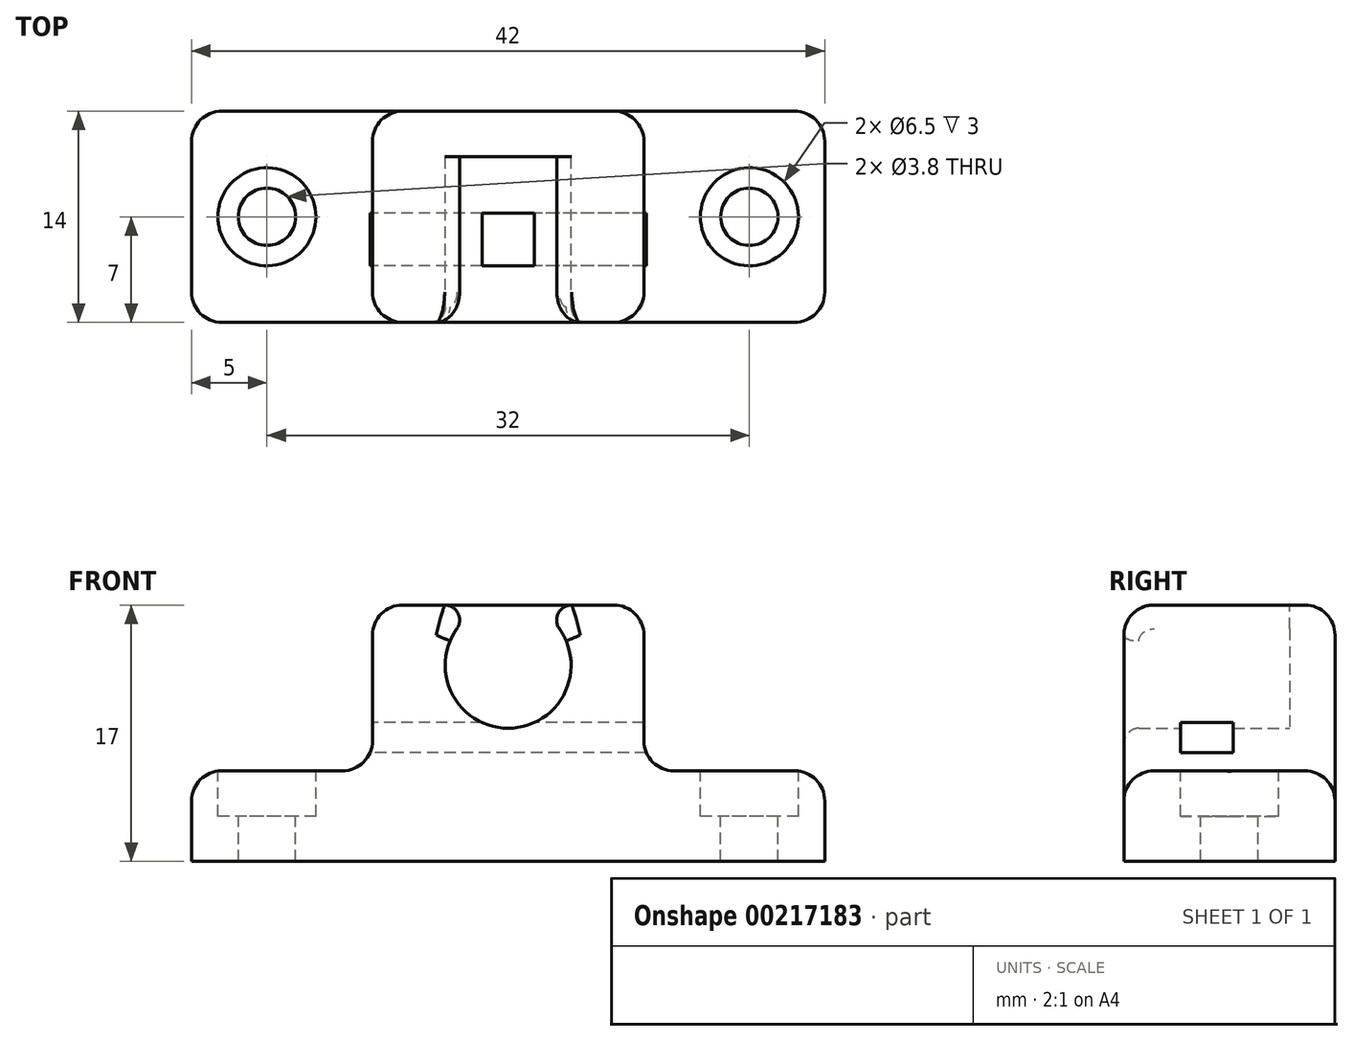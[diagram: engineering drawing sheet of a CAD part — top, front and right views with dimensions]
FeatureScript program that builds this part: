
annotation { "Feature Type Name" : "Feature", "Feature Type Description" : "" }
export const myFeature = defineFeature(function(context is Context, id is Id, definition is map)
    precondition{}
    {
        {
            var Q0;
            Q0=qCreatedBy(makeId("Front.planeOp"),FACE);
            var sketch = newSketch(context, id + "F0", { "sketchPlane" : qUnion([Q0])});
            skLineSegment(sketch, "E0", {"start": v(0, 0) * mm, "end": v(-21, 0) * mm});
            skLineSegment(sketch, "E1", {"start": v(-21, 0) * mm, "end": v(-21, 6) * mm});
            skLineSegment(sketch, "E2", {"start": v(-21, 6) * mm, "end": v(-9, 6) * mm});
            skLineSegment(sketch, "E3", {"start": v(-9, 6) * mm, "end": v(-9, 17) * mm});
            skLineSegment(sketch, "E4", {"start": v(-9, 17) * mm, "end": v(0, 17) * mm});
            skLineSegment(sketch, "E5.MirrorCS", {"start": v(0, 0) * mm, "end": v(21, 0) * mm});
            skLineSegment(sketch, "E6.MirrorCS", {"start": v(21, 6) * mm, "end": v(9, 6) * mm});
            skLineSegment(sketch, "E7.MirrorCS", {"start": v(9, 17) * mm, "end": v(0, 17) * mm});
            skLineSegment(sketch, "E8.MirrorCS", {"start": v(9, 6) * mm, "end": v(9, 17) * mm});
            skLineSegment(sketch, "E9.MirrorCS", {"start": v(21, 0) * mm, "end": v(21, 6) * mm});
            skCircle(sketch, "E10", {"center": v(0, 13) * mm, "radius": 4.17 * mm});
            skSolve(sketch);
        }
        {
            var Q0;
            Q0=makeQuery(id+"F0.imprint","IMPRINT",FACE,{"disambiguationData":[TD([[makeQuery(id+"F0.imprint","IMPRINT",EDGE,{"derivedFrom":sQuery(id+"F0.wireOp",EDGE,"E0")}),-1.0]])]});
            var Q1;
            {var subQ0=sQuery(id+"F0.wireOp",EDGE,"E7.MirrorCS");var subQ1=sQuery(id+"F0.wireOp",EDGE,"E4");var subQ2=makeQuery(id+"F0.imprint","INTERSECT",VERTEX,{"derivedFrom":[subQ1,subQ0]});Q1=makeQuery(id+"F0.imprint","IMPRINT",FACE,{"disambiguationData":[TD([[makeQuery(id+"F0.imprint","IMPRINT",EDGE,{"disambiguationData":[TD([[subQ2,1.0]])],"derivedFrom":subQ1}),-1.0]])]});}
            extrude(context, id + "F1", {"entities" : qUnion([Q0, Q1]), "oppositeDirection" : true, "depth" : 3 * mm});
        }
        {
            var Q0;
            Q0=makeQuery(id+"F0.imprint","IMPRINT",FACE,{"disambiguationData":[TD([[makeQuery(id+"F0.imprint","IMPRINT",EDGE,{"derivedFrom":sQuery(id+"F0.wireOp",EDGE,"E0")}),-1.0]])]});
            extrude(context, id + "F2", {"entities" : qUnion([Q0]), "operationType" : NewBodyOperationType.ADD, "depth" : 11 * mm});
        }
        {
            var Q0;
            {var subQ0=sQuery(id+"F0.wireOp",EDGE,"E3");Q0=makeQuery(id+"F2.boolean.opBoolean","MERGE",FACE,{"derivedFrom":[makeQuery(id+"F1.opExtrude","SWEPT_FACE",FACE,{"disambiguationData":[OSD([subQ0])]}),makeQuery(id+"F2.opExtrude","SWEPT_FACE",FACE,{"disambiguationData":[OSD([subQ0])]})]});}
            var sketch = newSketch(context, id + "F3", { "sketchPlane" : qUnion([Q0])});
            skLineSegment(sketch, "E11.bottom", {"start": v(3.75, 9.2) * mm, "end": v(7.25, 9.2) * mm});
            skLineSegment(sketch, "E11.top", {"start": v(3.75, 7.2) * mm, "end": v(7.25, 7.2) * mm});
            skLineSegment(sketch, "E11.left", {"start": v(3.75, 9.2) * mm, "end": v(3.75, 7.2) * mm});
            skLineSegment(sketch, "E11.right", {"start": v(7.25, 9.2) * mm, "end": v(7.25, 7.2) * mm});
            skSolve(sketch);
        }
        {
            var Q0;
            Q0=makeQuery(id+"F3.imprint","IMPRINT",FACE,{"disambiguationData":[TD([[makeQuery(id+"F3.imprint","IMPRINT",EDGE,{"derivedFrom":sQuery(id+"F3.wireOp",EDGE,"E11.bottom")}),-1.0]])]});
            extrude(context, id + "F4", {"entities" : qUnion([Q0]), "operationType" : NewBodyOperationType.REMOVE, "endBound" : BoundingType.THROUGH_ALL, "oppositeDirection" : true, "depth" : 25 * mm});
        }
        {
            var Q0;
            {var subQ0=sQuery(id+"F0.wireOp",EDGE,"E2");Q0=makeQuery(id+"F2.boolean.opBoolean","MERGE",FACE,{"derivedFrom":[makeQuery(id+"F1.opExtrude","SWEPT_FACE",FACE,{"disambiguationData":[OSD([subQ0])]}),makeQuery(id+"F2.opExtrude","SWEPT_FACE",FACE,{"disambiguationData":[OSD([subQ0])]})]});}
            var sketch = newSketch(context, id + "F5", { "sketchPlane" : qUnion([Q0])});
            skCircle(sketch, "E12", {"center": v(-16, -4) * mm, "radius": 3.25 * mm});
            skPoint(sketch, "E12.centerSnap0", {"position": v(-21, -4) * mm});
            skCircle(sketch, "E13", {"center": v(-16, -4) * mm, "radius": 1.9 * mm});
            skSolve(sketch);
        }
        {
            var Q0;
            {var subQ0=sQuery(id+"F0.wireOp",EDGE,"E6.MirrorCS");Q0=makeQuery(id+"F2.boolean.opBoolean","MERGE",FACE,{"derivedFrom":[makeQuery(id+"F1.opExtrude","SWEPT_FACE",FACE,{"disambiguationData":[OSD([subQ0])]}),makeQuery(id+"F2.opExtrude","SWEPT_FACE",FACE,{"disambiguationData":[OSD([subQ0])]})]});}
            var sketch = newSketch(context, id + "F6", { "sketchPlane" : qUnion([Q0])});
            skCircle(sketch, "E14", {"center": v(16, -4) * mm, "radius": 3.25 * mm});
            skPoint(sketch, "E14.centerSnap0", {"position": v(21, -4) * mm});
            skCircle(sketch, "E15", {"center": v(16, -4) * mm, "radius": 1.9 * mm});
            skSolve(sketch);
        }
        {
            var Q0;
            Q0=makeQuery(id+"F5.imprint","IMPRINT",FACE,{"disambiguationData":[TD([[makeQuery(id+"F5.imprint","IMPRINT",EDGE,{"derivedFrom":sQuery(id+"F5.wireOp",EDGE,"E12")}),1.0]])]});
            var Q1;
            Q1=makeQuery(id+"F6.imprint","IMPRINT",FACE,{"disambiguationData":[TD([[makeQuery(id+"F6.imprint","IMPRINT",EDGE,{"derivedFrom":sQuery(id+"F6.wireOp",EDGE,"E14")}),1.0]])]});
            extrude(context, id + "F7", {"entities" : qUnion([Q0, Q1]), "operationType" : NewBodyOperationType.REMOVE, "oppositeDirection" : true, "depth" : 3 * mm});
        }
        {
            var Q0;
            {var subQ0=sQuery(id+"F0.wireOp",EDGE,"E2");Q0=makeQuery(id+"F7.boolean.opBoolean","SPLIT",FACE,{"disambiguationData":[TD([makeQuery(id+"F7.opExtrude","SWEPT_FACE",FACE,{"disambiguationData":[OSD([sQuery(id+"F5.wireOp",EDGE,"E13")])]})])],"derivedFrom":makeQuery(id+"F2.boolean.opBoolean","MERGE",FACE,{"derivedFrom":[makeQuery(id+"F1.opExtrude","SWEPT_FACE",FACE,{"disambiguationData":[OSD([subQ0])]}),makeQuery(id+"F2.opExtrude","SWEPT_FACE",FACE,{"disambiguationData":[OSD([subQ0])]})]})});}
            var Q1;
            {var subQ0=sQuery(id+"F0.wireOp",EDGE,"E6.MirrorCS");Q1=makeQuery(id+"F7.boolean.opBoolean","SPLIT",FACE,{"disambiguationData":[TD([makeQuery(id+"F7.opExtrude","SWEPT_FACE",FACE,{"disambiguationData":[OSD([sQuery(id+"F6.wireOp",EDGE,"E15")])]})])],"derivedFrom":makeQuery(id+"F2.boolean.opBoolean","MERGE",FACE,{"derivedFrom":[makeQuery(id+"F1.opExtrude","SWEPT_FACE",FACE,{"disambiguationData":[OSD([subQ0])]}),makeQuery(id+"F2.opExtrude","SWEPT_FACE",FACE,{"disambiguationData":[OSD([subQ0])]})]})});}
            extrude(context, id + "F8", {"entities" : qUnion([Q0, Q1]), "operationType" : NewBodyOperationType.REMOVE, "oppositeDirection" : true, "depth" : 25 * mm});
        }
        {
            var Q0;
            Q0=makeQuery(id+"F2.opExtrude","CAP_EDGE",EDGE,{"disambiguationData":[OSD([sQuery(id+"F0.wireOp",EDGE,"E1")])],"isStart":false});
            var Q1;
            Q1=makeQuery(id+"F2.opExtrude","CAP_EDGE",EDGE,{"disambiguationData":[OSD([sQuery(id+"F0.wireOp",EDGE,"E2")])],"isStart":false});
            var Q2;
            Q2=makeQuery(id+"F2.opExtrude","CAP_EDGE",EDGE,{"disambiguationData":[OSD([sQuery(id+"F0.wireOp",EDGE,"E3")])],"isStart":false});
            var Q3;
            Q3=makeQuery(id+"F2.opExtrude","CAP_EDGE",EDGE,{"disambiguationData":[OSD([sQuery(id+"F0.wireOp",EDGE,"E4")])],"isStart":false});
            var Q4;
            {var subQ0=sQuery(id+"F0.wireOp",EDGE,"E4");var subQ1=sQuery(id+"F0.wireOp",EDGE,"E3");Q4=makeQuery(id+"F2.boolean.opBoolean","MERGE",EDGE,{"derivedFrom":[makeQuery(id+"F1.opExtrude","SWEPT_EDGE",EDGE,{"disambiguationData":[OSD([subQ1,subQ0])]}),makeQuery(id+"F2.opExtrude","SWEPT_EDGE",EDGE,{"disambiguationData":[OSD([subQ1,subQ0])]})]});}
            var Q5;
            Q5=makeQuery(id+"F1.opExtrude","CAP_EDGE",EDGE,{"disambiguationData":[OSD([sQuery(id+"F0.wireOp",EDGE,"E4"),sQuery(id+"F0.wireOp",EDGE,"E7.MirrorCS")])],"isStart":false});
            var Q6;
            {var subQ0=sQuery(id+"F0.wireOp",EDGE,"E8.MirrorCS");var subQ1=sQuery(id+"F0.wireOp",EDGE,"E7.MirrorCS");Q6=makeQuery(id+"F2.boolean.opBoolean","MERGE",EDGE,{"derivedFrom":[makeQuery(id+"F1.opExtrude","SWEPT_EDGE",EDGE,{"disambiguationData":[OSD([subQ1,subQ0])]}),makeQuery(id+"F2.opExtrude","SWEPT_EDGE",EDGE,{"disambiguationData":[OSD([subQ1,subQ0])]})]});}
            var Q7;
            {var subQ0=sQuery(id+"F0.wireOp",EDGE,"E2");var subQ1=sQuery(id+"F0.wireOp",EDGE,"E1");Q7=makeQuery(id+"F2.boolean.opBoolean","MERGE",EDGE,{"derivedFrom":[makeQuery(id+"F1.opExtrude","SWEPT_EDGE",EDGE,{"disambiguationData":[OSD([subQ1,subQ0])]}),makeQuery(id+"F2.opExtrude","SWEPT_EDGE",EDGE,{"disambiguationData":[OSD([subQ1,subQ0])]})]});}
            var Q8;
            Q8=makeQuery(id+"F1.opExtrude","CAP_EDGE",EDGE,{"disambiguationData":[OSD([sQuery(id+"F0.wireOp",EDGE,"E2")])],"isStart":false});
            var Q9;
            Q9=makeQuery(id+"F2.opExtrude","CAP_EDGE",EDGE,{"disambiguationData":[OSD([sQuery(id+"F0.wireOp",EDGE,"E7.MirrorCS")])],"isStart":false});
            var Q10;
            Q10=makeQuery(id+"F2.opExtrude","CAP_EDGE",EDGE,{"disambiguationData":[OSD([sQuery(id+"F0.wireOp",EDGE,"E8.MirrorCS")])],"isStart":false});
            var Q11;
            Q11=makeQuery(id+"F2.opExtrude","CAP_EDGE",EDGE,{"disambiguationData":[OSD([sQuery(id+"F0.wireOp",EDGE,"E6.MirrorCS")])],"isStart":false});
            var Q12;
            {var subQ0=sQuery(id+"F0.wireOp",EDGE,"E9.MirrorCS");var subQ1=sQuery(id+"F0.wireOp",EDGE,"E6.MirrorCS");Q12=makeQuery(id+"F2.boolean.opBoolean","MERGE",EDGE,{"derivedFrom":[makeQuery(id+"F1.opExtrude","SWEPT_EDGE",EDGE,{"disambiguationData":[OSD([subQ1,subQ0])]}),makeQuery(id+"F2.opExtrude","SWEPT_EDGE",EDGE,{"disambiguationData":[OSD([subQ1,subQ0])]})]});}
            var Q13;
            {var subQ0=sQuery(id+"F0.wireOp",EDGE,"E8.MirrorCS");var subQ1=sQuery(id+"F0.wireOp",EDGE,"E6.MirrorCS");Q13=makeQuery(id+"F2.boolean.opBoolean","MERGE",EDGE,{"derivedFrom":[makeQuery(id+"F1.opExtrude","SWEPT_EDGE",EDGE,{"disambiguationData":[OSD([subQ1,subQ0])]}),makeQuery(id+"F2.opExtrude","SWEPT_EDGE",EDGE,{"disambiguationData":[OSD([subQ1,subQ0])]})]});}
            var Q14;
            {var subQ0=sQuery(id+"F0.wireOp",EDGE,"E3");var subQ1=sQuery(id+"F0.wireOp",EDGE,"E2");Q14=makeQuery(id+"F2.boolean.opBoolean","MERGE",EDGE,{"derivedFrom":[makeQuery(id+"F1.opExtrude","SWEPT_EDGE",EDGE,{"disambiguationData":[OSD([subQ1,subQ0])]}),makeQuery(id+"F2.opExtrude","SWEPT_EDGE",EDGE,{"disambiguationData":[OSD([subQ1,subQ0])]})]});}
            var Q15;
            Q15=makeQuery(id+"F2.opExtrude","CAP_EDGE",EDGE,{"disambiguationData":[OSD([sQuery(id+"F0.wireOp",EDGE,"E9.MirrorCS")])],"isStart":false});
            var Q16;
            Q16=makeQuery(id+"F1.opExtrude","CAP_EDGE",EDGE,{"disambiguationData":[OSD([sQuery(id+"F0.wireOp",EDGE,"E9.MirrorCS")])],"isStart":false});
            var Q17;
            Q17=makeQuery(id+"F1.opExtrude","CAP_EDGE",EDGE,{"disambiguationData":[OSD([sQuery(id+"F0.wireOp",EDGE,"E6.MirrorCS")])],"isStart":false});
            var Q18;
            Q18=makeQuery(id+"F1.opExtrude","CAP_EDGE",EDGE,{"disambiguationData":[OSD([sQuery(id+"F0.wireOp",EDGE,"E8.MirrorCS")])],"isStart":false});
            var Q19;
            Q19=makeQuery(id+"F1.opExtrude","CAP_EDGE",EDGE,{"disambiguationData":[OSD([sQuery(id+"F0.wireOp",EDGE,"E3")])],"isStart":false});
            var Q20;
            Q20=makeQuery(id+"F1.opExtrude","CAP_EDGE",EDGE,{"disambiguationData":[OSD([sQuery(id+"F0.wireOp",EDGE,"E1")])],"isStart":false});
            fillet(context, id + "F9", {"entities" : qUnion([Q0, Q1, Q2, Q3, Q4, Q5, Q6, Q7, Q8, Q9, Q10, Q11, Q12, Q13, Q14, Q15, Q16, Q17, Q18, Q19, Q20]), "radius" : 2 * mm, "tangentPropagation" : true, "allowEdgeOverflow" : false});
        }
        {
            var Q0;
            Q0=makeQuery(id+"F2.opExtrude","SWEPT_EDGE",EDGE,{"disambiguationData":[OSD([sQuery(id+"F0.wireOp",EDGE,"E7.MirrorCS"),sQuery(id+"F0.wireOp",EDGE,"E10")])]});
            var Q1;
            Q1=makeQuery(id+"F2.opExtrude","SWEPT_EDGE",EDGE,{"disambiguationData":[OSD([sQuery(id+"F0.wireOp",EDGE,"E4"),sQuery(id+"F0.wireOp",EDGE,"E10")])]});
            fillet(context, id + "F10", {"entities" : qUnion([Q0, Q1]), "radius" : 1 * mm, "tangentPropagation" : true, "allowEdgeOverflow" : false});
        }
    });
